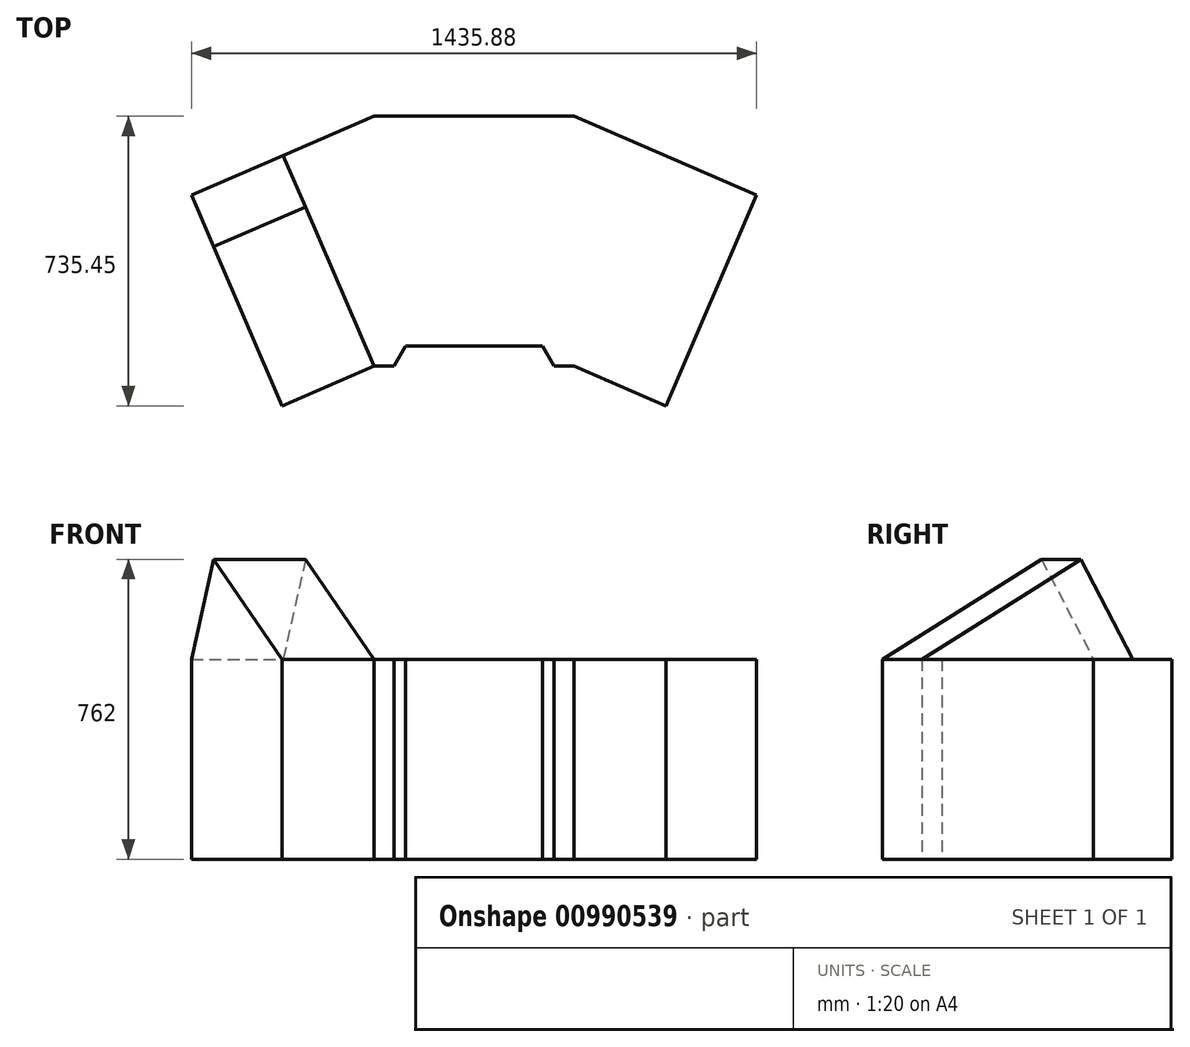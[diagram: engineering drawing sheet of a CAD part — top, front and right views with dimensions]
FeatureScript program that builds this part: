
annotation { "Feature Type Name" : "Feature", "Feature Type Description" : "" }
export const myFeature = defineFeature(function(context is Context, id is Id, definition is map)
    precondition{}
    {
        {
            var Q0;
            Q0=qCreatedBy(makeId("Top.planeOp"),FACE);
            var sketch = newSketch(context, id + "F0", { "sketchPlane" : qUnion([Q0])});
            skLineSegment(sketch, "E0.bottom", {"start": v(0, 0) * mm, "end": v(508, 0) * mm});
            skLineSegment(sketch, "E0.top", {"start": v(0, 635) * mm, "end": v(508, 635) * mm});
            skLineSegment(sketch, "E0.left", {"start": v(0, 0) * mm, "end": v(0, 635) * mm});
            skLineSegment(sketch, "E0.right", {"start": v(508, 0) * mm, "end": v(508, 635) * mm});
            skLineSegment(sketch, "E1", {"start": v(0, 0) * mm, "end": v(-233.3, -100.45) * mm});
            skLineSegment(sketch, "E2", {"start": v(-233.3, -100.45) * mm, "end": v(-463.94, 435.25) * mm});
            skLineSegment(sketch, "E3", {"start": v(-463.94, 435.25) * mm, "end": v(0, 635) * mm});
            skLineSegment(sketch, "E4", {"start": v(254, 0) * mm, "end": v(254, 635) * mm});
            skLineSegment(sketch, "E5.MirrorCS", {"start": v(971.94, 435.25) * mm, "end": v(508, 635) * mm});
            skLineSegment(sketch, "E6.MirrorCS", {"start": v(741.3, -100.45) * mm, "end": v(971.94, 435.25) * mm});
            skLineSegment(sketch, "E7.MirrorCS", {"start": v(508, 0) * mm, "end": v(741.3, -100.45) * mm});
            skLineSegment(sketch, "E8", {"start": v(50.8, 0) * mm, "end": v(80.13, 50.8) * mm});
            skLineSegment(sketch, "E9", {"start": v(80.13, 50.8) * mm, "end": v(427.87, 50.8) * mm});
            skLineSegment(sketch, "E10", {"start": v(427.87, 50.8) * mm, "end": v(457.2, 0) * mm});
            skSolve(sketch);
        }
        {
            var Q0;
            Q0=makeQuery(id+"F0.imprint","IMPRINT",FACE,{"disambiguationData":[TD([[makeQuery(id+"F0.imprint","IMPRINT",EDGE,{"derivedFrom":sQuery(id+"F0.wireOp",EDGE,"E0.left")}),1.0]])]});
            var Q1;
            {var subQ5=sQuery(id+"F0.wireOp",EDGE,"E0.left");Q1=makeQuery(id+"F0.imprint","IMPRINT",FACE,{"disambiguationData":[TD([[makeQuery(id+"F0.imprint","IMPRINT",EDGE,{"derivedFrom":subQ5}),-1.0]])]});}
            var Q2;
            {var subQ5=sQuery(id+"F0.wireOp",EDGE,"E0.right");Q2=makeQuery(id+"F0.imprint","IMPRINT",FACE,{"disambiguationData":[TD([[makeQuery(id+"F0.imprint","IMPRINT",EDGE,{"derivedFrom":subQ5}),1.0]])]});}
            var Q3;
            Q3=makeQuery(id+"F0.imprint","IMPRINT",FACE,{"disambiguationData":[TD([[makeQuery(id+"F0.imprint","IMPRINT",EDGE,{"derivedFrom":sQuery(id+"F0.wireOp",EDGE,"E0.right")}),-1.0]])]});
            extrude(context, id + "F1", {"entities" : qUnion([Q0, Q1, Q2, Q3]), "depth" : 508 * mm, "offsetDistance" : 25.4 * mm});
        }
        {
            var Q0;
            Q0=makeQuery(id+"F1.opExtrude","SWEPT_FACE",FACE,{"disambiguationData":[OSD([sQuery(id+"F0.wireOp",EDGE,"E2")])]});
            var sketch = newSketch(context, id + "F2", { "sketchPlane" : qUnion([Q0])});
            skLineSegment(sketch, "E11", {"start": v(0, 508) * mm, "end": v(-439.94, 762) * mm});
            skLineSegment(sketch, "E12", {"start": v(-439.94, 762) * mm, "end": v(-583.24, 508) * mm});
            skSolve(sketch);
        }
        {
            var Q0;
            Q0=makeQuery(id+"F2.imprint","IMPRINT",FACE,{"disambiguationData":[TD([[makeQuery(id+"F2.imprint","IMPRINT",EDGE,{"derivedFrom":sQuery(id+"F2.wireOp",EDGE,"E11")}),1.0]])]});
            extrude(context, id + "F3", {"entities" : qUnion([Q0]), "operationType" : NewBodyOperationType.ADD, "oppositeDirection" : true, "depth" : 254 * mm, "offsetDistance" : 25.4 * mm});
        }
    });
